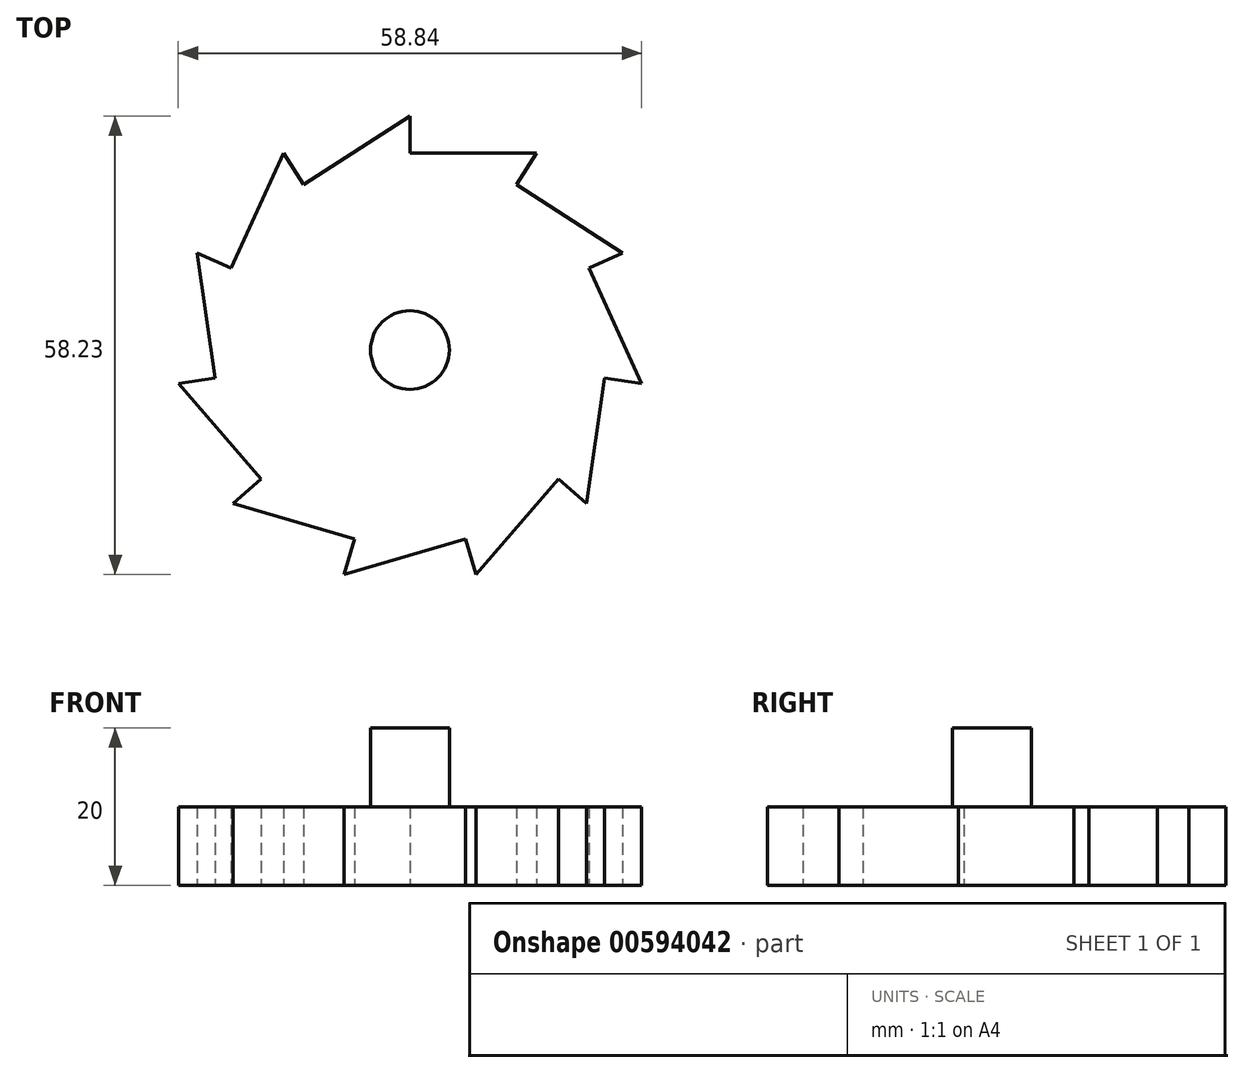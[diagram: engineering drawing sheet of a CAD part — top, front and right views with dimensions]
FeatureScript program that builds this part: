
annotation { "Feature Type Name" : "Feature", "Feature Type Description" : "" }
export const myFeature = defineFeature(function(context is Context, id is Id, definition is map)
    precondition{}
    {
        {
            var Q0;
            Q0=qCreatedBy(makeId("Top.planeOp"),FACE);
            var sketch = newSketch(context, id + "F0", { "sketchPlane" : qUnion([Q0])});
            skCircle(sketch, "E0", {"center": v(0, 0) * mm, "radius": 30 * mm});
            skLineSegment(sketch, "E1", {"start": v(0, 30) * mm, "end": v(0, 25) * mm});
            skLineSegment(sketch, "E2", {"start": v(0, 25) * mm, "end": v(16.58, 25) * mm});
            skLineSegment(sketch, "E3.1.0", {"start": v(-13.52, 21.03) * mm, "end": v(0.43, 30) * mm});
            skLineSegment(sketch, "E3.1.1", {"start": v(-16.22, 25.24) * mm, "end": v(-13.52, 21.03) * mm});
            skLineSegment(sketch, "E3.2.0", {"start": v(-22.74, 10.39) * mm, "end": v(-15.85, 25.47) * mm});
            skLineSegment(sketch, "E3.2.1", {"start": v(-27.29, 12.46) * mm, "end": v(-22.74, 10.39) * mm});
            skLineSegment(sketch, "E3.3.0", {"start": v(-24.75, -3.56) * mm, "end": v(-27.1, 12.86) * mm});
            skLineSegment(sketch, "E3.3.1", {"start": v(-29.7, -4.27) * mm, "end": v(-24.75, -3.56) * mm});
            skLineSegment(sketch, "E3.4.0", {"start": v(-18.9, -16.37) * mm, "end": v(-29.75, -3.84) * mm});
            skLineSegment(sketch, "E3.4.1", {"start": v(-22.67, -19.65) * mm, "end": v(-18.9, -16.37) * mm});
            skLineSegment(sketch, "E3.5.0", {"start": v(-7.04, -23.99) * mm, "end": v(-22.95, -19.32) * mm});
            skLineSegment(sketch, "E3.5.1", {"start": v(-8.45, -28.78) * mm, "end": v(-7.04, -23.99) * mm});
            skCircle(sketch, "E3.5.2", {"center": v(0, 0) * mm, "radius": 30 * mm, "construction": true});
            skLineSegment(sketch, "E3.6.0", {"start": v(7.04, -23.99) * mm, "end": v(-8.87, -28.66) * mm});
            skLineSegment(sketch, "E3.6.1", {"start": v(8.45, -28.78) * mm, "end": v(7.04, -23.99) * mm});
            skLineSegment(sketch, "E3.7.0", {"start": v(18.9, -16.37) * mm, "end": v(8.03, -28.9) * mm});
            skLineSegment(sketch, "E3.7.1", {"start": v(22.67, -19.65) * mm, "end": v(18.9, -16.37) * mm});
            skLineSegment(sketch, "E3.8.0", {"start": v(24.75, -3.56) * mm, "end": v(22.39, -19.97) * mm});
            skLineSegment(sketch, "E3.8.1", {"start": v(29.7, -4.27) * mm, "end": v(24.75, -3.56) * mm});
            skLineSegment(sketch, "E3.9.0", {"start": v(22.74, 10.39) * mm, "end": v(29.63, -4.7) * mm});
            skLineSegment(sketch, "E3.9.1", {"start": v(27.29, 12.46) * mm, "end": v(22.74, 10.39) * mm});
            skLineSegment(sketch, "E3.10.0", {"start": v(13.52, 21.03) * mm, "end": v(27.47, 12.07) * mm});
            skLineSegment(sketch, "E3.10.1", {"start": v(16.22, 25.24) * mm, "end": v(13.52, 21.03) * mm});
            skCircle(sketch, "E4", {"center": v(0, 0) * mm, "radius": 5 * mm});
            skSolve(sketch);
        }
        {
            var Q0;
            Q0=makeQuery(id+"F0.imprint","IMPRINT",FACE,{"disambiguationData":[TD([[makeQuery(id+"F0.imprint","IMPRINT",EDGE,{"derivedFrom":sQuery(id+"F0.wireOp",EDGE,"E4")}),-1.0]])]});
            extrude(context, id + "F1", {"entities" : qUnion([Q0]), "depth" : 10 * mm, "offsetDistance" : 25 * mm});
        }
        {
            var Q0;
            Q0=makeQuery(id+"F0.imprint","IMPRINT",FACE,{"disambiguationData":[TD([[makeQuery(id+"F0.imprint","IMPRINT",EDGE,{"derivedFrom":sQuery(id+"F0.wireOp",EDGE,"E4")}),1.0]])]});
            extrude(context, id + "F2", {"entities" : qUnion([Q0]), "operationType" : NewBodyOperationType.ADD, "depth" : 20 * mm, "offsetDistance" : 25 * mm});
        }
    });
